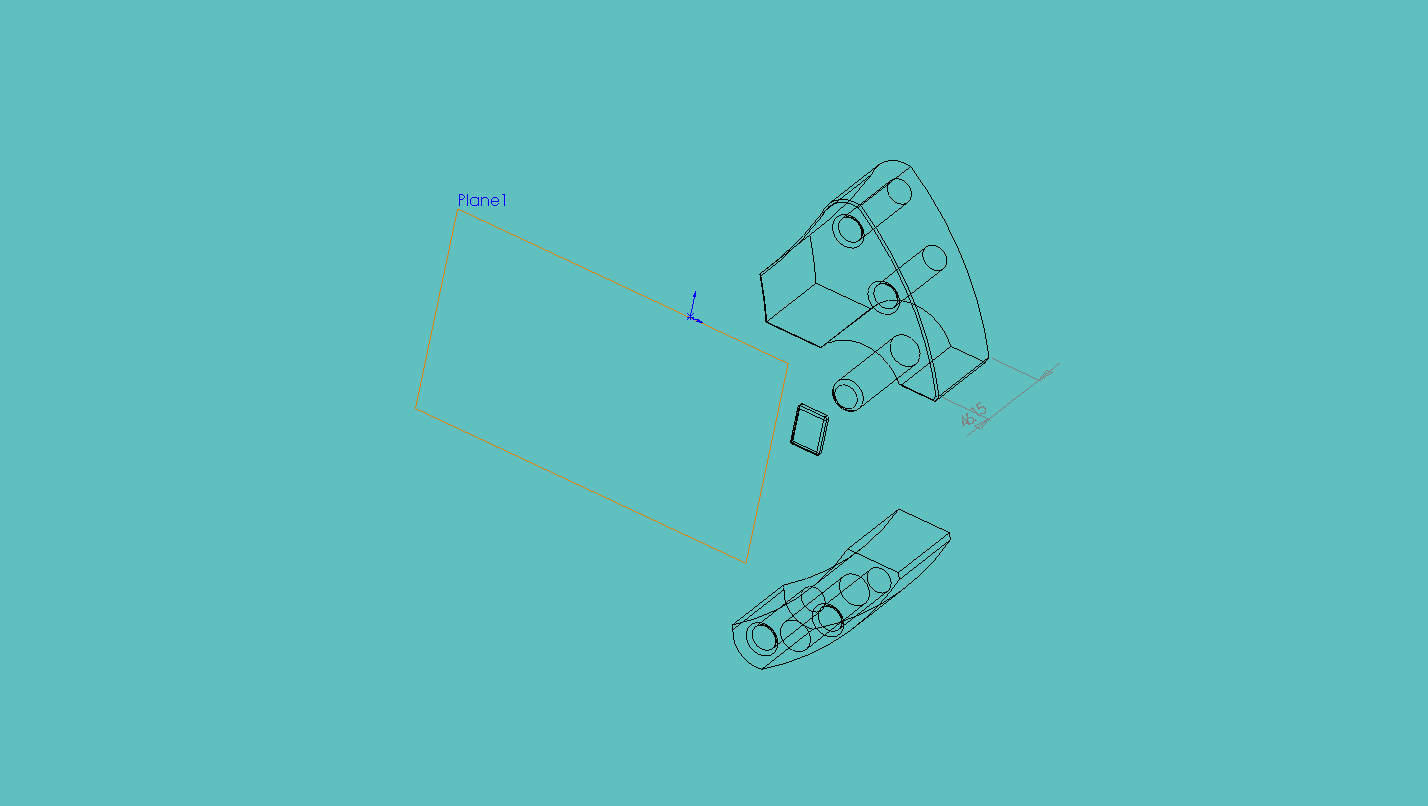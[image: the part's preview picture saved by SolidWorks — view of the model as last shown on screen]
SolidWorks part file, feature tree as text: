
SOLIDWORKS PART (.sldprt)
format: sldprt  version: not decoded by parser v0  size: 611,840 bytes
history: native  units: mm
features: sketch x10, fillet x7, cut_extrude x6, extrude x4, chamfer x2, material x1, plane x1 + 1 further entry (+12 scaffold rows collapsed)
feature tree (44):
  "Annotations"  RD1=46.15mm
  scaffold x12  (default folders/planes/origin — collapsed)
  material  "Material <not specified>"
  sketch  "Sketch3"
  extrude  "Extrude1"  Depth=47.15mm
  sketch  "Sketch5"
  extrude  "Extrude2"  Depth=44.45mm
  sketch  "Sketch6"  dims[c1.D1=12.7mm c1.D2=12.7mm c2.D1=~13.906952mm c2.D2=25.0mm c2.D3=25.0mm]
  cut_extrude  "Cut-Extrude1"  [1 undecoded]
  fillet  "Fillet2"  Radius=2mm
  fillet  "Fillet3"  Radius=2mm
  fillet  "Fillet4"  Radius=2mm
  sketch  "Sketch8"
  cut_extrude  "Cut-Extrude3"  [1 undecoded]
  chamfer  "Chamfer2"  Distance=1mm Angle=45deg
  sketch  "Sketch9"  dims[D1=279.4mm D2=177.8mm D3=~94.511865mm]
  cut_extrude  "Cut-Extrude4"  Depth=50mm
  plane  "Plane1"  Offset=10mm
  sketch  "Sketch11"  dims[D1=50.0mm]
  cut_extrude  "Cut-Extrude6"  [1 undecoded]
  sketch  "Sketch12"
  cut_extrude  "Cut-Extrude7"  Depth=20mm
  sketch  "Sketch13"
  extrude  "Extrude3"  Depth=20mm
  fillet  "Fillet5"  Radius=2mm
  sketch  "Sketch14"
  extrude  "Extrude4"  Depth=3mm
  fillet  "Fillet6"  Radius=1mm
  fillet  "Fillet7"  Radius=1mm
  fillet  "Fillet8"  Radius=1mm
  sketch  "Sketch15"  dims[c1.D1=4.75mm c1.D2=4.75mm c2.D1=~9.532299mm c2.D2=~35.322241mm]
  cut_extrude  "Cut-Extrude8"  Depth=30mm
  chamfer  "Chamfer3"  Distance=1mm Angle=45deg
decode coverage: 20 of 29 modeling features carry decoded parameters; 1 rows unclassified (native names shown)
note: ~ marks probable driven/reference dimensions
note: 3 parameter values undecoded
summary: no parameter record found for 3 features
note: suppression state not decoded; provenance and decode notes live in map.json
